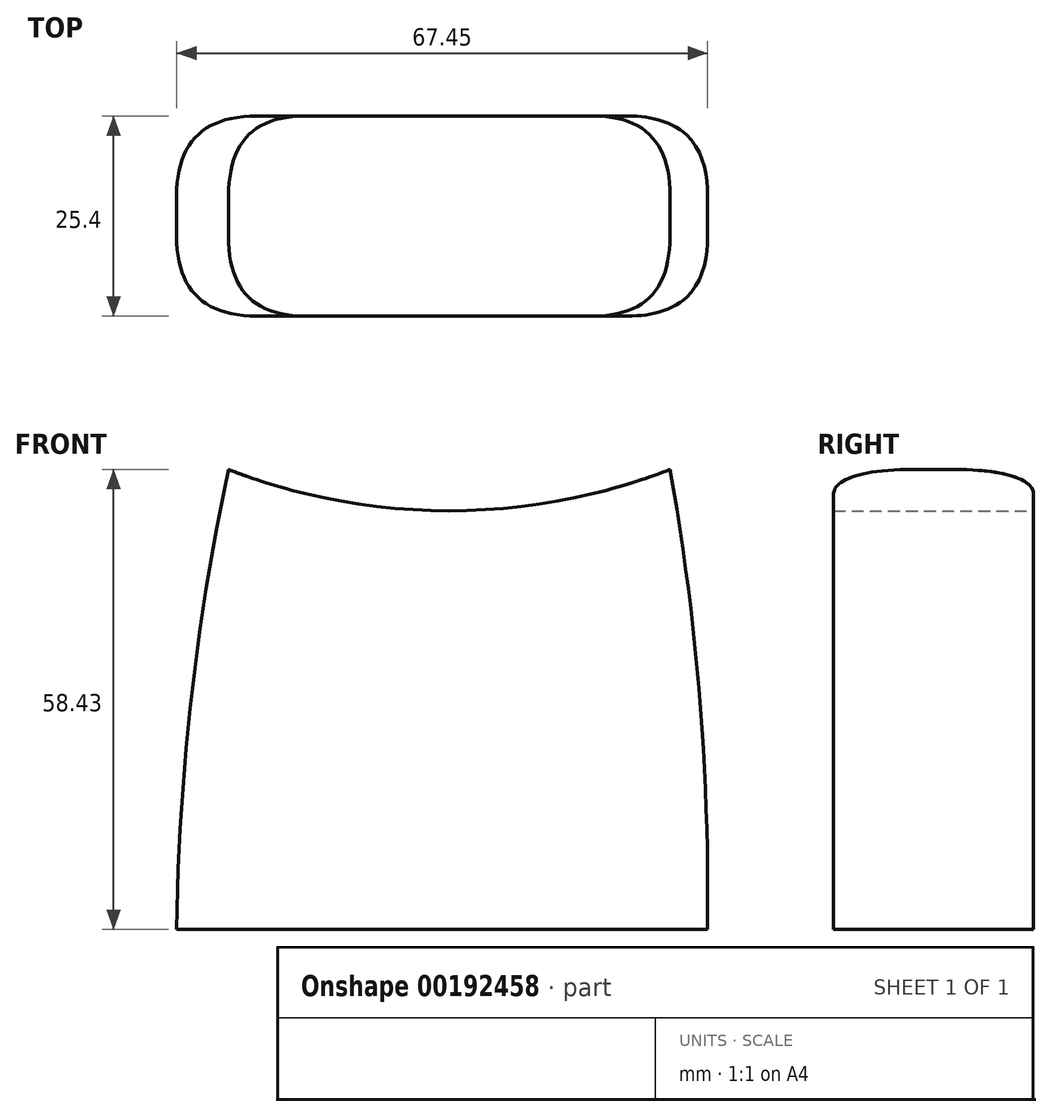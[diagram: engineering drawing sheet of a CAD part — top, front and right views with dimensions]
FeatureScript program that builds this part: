
annotation { "Feature Type Name" : "Feature", "Feature Type Description" : "" }
export const myFeature = defineFeature(function(context is Context, id is Id, definition is map)
    precondition{}
    {
        {
            var Q0;
            Q0=qCreatedBy(makeId("Front.planeOp"),FACE);
            var sketch = newSketch(context, id + "F0", { "sketchPlane" : qUnion([Q0])});
            skLineSegment(sketch, "E0", {"start": v(-39.12, -58.43) * mm, "end": v(28.3, -58.43) * mm});
            skArc(sketch, "E1", {"start": v(-32.53, 0) * mm, "mid": v(-37.26, -29.05) * mm, "end": v(-39.12, -58.43) * mm});
            skArc(sketch, "E2", {"start": v(-32.53, 0) * mm, "mid": v(-4.5, -5.24) * mm, "end": v(23.55, 0) * mm});
            skArc(sketch, "E3", {"start": v(28.3, -58.43) * mm, "mid": v(27.33, -29.1) * mm, "end": v(23.55, 0) * mm});
            skSolve(sketch);
        }
        {
            var Q0;
            Q0=makeQuery(id+"F0.imprint","IMPRINT",FACE,{"disambiguationData":[TD([[makeQuery(id+"F0.imprint","IMPRINT",EDGE,{"derivedFrom":sQuery(id+"F0.wireOp",EDGE,"E0")}),1.0]])]});
            extrude(context, id + "F1", {"entities" : qUnion([Q0]), "depth" : 25.4 * mm});
        }
        {
            var Q0;
            Q0=makeQuery(id+"F1.opExtrude","CAP_EDGE",EDGE,{"disambiguationData":[OSD([sQuery(id+"F0.wireOp",EDGE,"E1")])],"isStart":true});
            var Q1;
            Q1=makeQuery(id+"F1.opExtrude","CAP_EDGE",EDGE,{"disambiguationData":[OSD([sQuery(id+"F0.wireOp",EDGE,"E1")])],"isStart":false});
            fillet(context, id + "F2", {"entities" : qUnion([Q0, Q1]), "radius" : 10.16 * mm, "rho" : 0.5, "crossSection" : FilletCrossSection.CONIC, "allowEdgeOverflow" : false});
        }
        {
            var Q0;
            Q0=makeQuery(id+"F1.opExtrude","CAP_EDGE",EDGE,{"disambiguationData":[OSD([sQuery(id+"F0.wireOp",EDGE,"E3")])],"isStart":false});
            var Q1;
            Q1=makeQuery(id+"F1.opExtrude","CAP_EDGE",EDGE,{"disambiguationData":[OSD([sQuery(id+"F0.wireOp",EDGE,"E3")])],"isStart":true});
            fillet(context, id + "F3", {"entities" : qUnion([Q0, Q1]), "radius" : 10.16 * mm, "rho" : 0.5, "crossSection" : FilletCrossSection.CONIC, "allowEdgeOverflow" : false});
        }
    });
